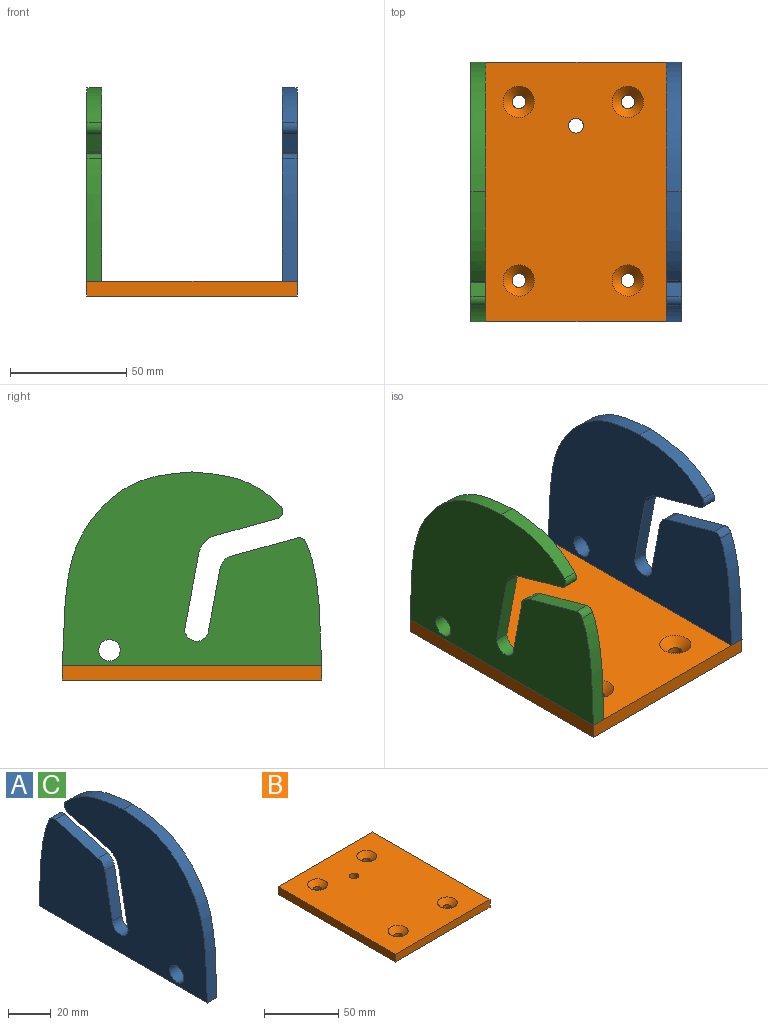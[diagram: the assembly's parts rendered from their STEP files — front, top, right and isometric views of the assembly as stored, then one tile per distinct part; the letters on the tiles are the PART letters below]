
ASSEMBLY  parts=3 mates=2
PART A: 16 faces, bbox 6.4x111.8x83.3 mm
  f0: cylinder r=3.17mm len=6.35mm, axis (-1,0,0), area 41.8mm2, adj f1,f13,f14,f15
  f1: extruded ~38.25x14.72mm, area 267.7mm2, adj f0,f2,f14,f15
  f2: extruded ~83.31x55.88mm, area 730.4mm2, adj f1,f3,f14,f15
  f3: plane 111.76x6.35mm, normal (0,0,-1), area 709.7mm2, adj f2,f4,f14,f15
  f4: extruded ~53.13x6.85mm, area 342.3mm2, adj f3,f5,f14,f15
  f5: cylinder r=3.17mm len=6.35mm, axis (-1,0,0), area 28.5mm2, adj f4,f6,f14,f15
  f6: plane 28.54x7.91mm, normal (0,-0.27,0.96), area 188mm2, adj f5,f7,f14,f15
  f7: cylinder r=6.35mm len=6.35mm, axis (-1,0,0), area 44.9mm2, adj f6,f8,f14,f15
  f8: plane 26.4x6.35mm, normal (0,-0.98,0.18), area 170.6mm2, adj f7,f9,f14,f15
  f9: cylinder r=5.21mm len=10.41mm, axis (-1,0,0), area 103.9mm2, adj f8,f10,f14,f15
  f10: plane 32.79x6.35mm, normal (0,0.98,-0.18), area 211.8mm2, adj f9,f11,f14,f15
  f11: cylinder r=9.53mm len=7.42mm, axis (-1,0,0), area 67.4mm2, adj f10,f13,f14,f15
  f12: cylinder r=4.64mm len=9.27mm, axis (-1,0,0), area 184.9mm2, adj f14,f15
  f13: plane 27.02x7.49mm, normal (0,0.27,-0.96), area 178mm2, adj f0,f11,f14,f15
  f14: plane 111.76x83.31mm, normal (1,0,0), area 7040.6mm2, adj f0,f1,f2,f3,f4,f5,f6,f7
  f15: plane 111.76x83.31mm, normal (-1,0,0), area 7040.6mm2, adj f0,f1,f2,f3,f4,f5,f6,f7
PART B: 15 faces, bbox 90.6x111.8x6.4 mm
  f0: plane 90.55x6.35mm, normal (0,-1,0), area 575mm2, adj f1,f8,f9,f10
  f1: plane 111.76x6.35mm, normal (1,0,0), area 709.7mm2, adj f0,f2,f9,f10
  f2: plane 90.55x6.35mm, normal (0,1,0), area 575mm2, adj f1,f8,f9,f10
  f3: cylinder r=2.92mm len=5.84mm, axis (0,0,-1), area 46.6mm2, adj f10,f14
  f4: cylinder r=2.92mm len=5.84mm, axis (0,0,-1), area 46.6mm2, adj f10,f12
  f5: cylinder r=2.92mm len=5.84mm, axis (0,0,-1), area 46.6mm2, adj f10,f13
  f6: cylinder r=2.92mm len=5.84mm, axis (0,0,-1), area 46.6mm2, adj f10,f11
  f7: cylinder r=3.17mm len=6.35mm, axis (0,0,-1), area 126.7mm2, adj f9,f10
  f8: plane 111.76x6.35mm, normal (-1,0,0), area 709.7mm2, adj f0,f2,f9,f10
  f9: plane 111.76x90.55mm, normal (0,0,1), area 9519mm2, adj f0,f1,f2,f7,f8,f11,f12,f13
  f10: plane 111.76x90.55mm, normal (0,0,-1), area 9981.1mm2, adj f0,f1,f2,f3,f4,f5,f6,f7
  f11: cone r=2.92mm half-angle=45deg, axis (0,0,1), area 163.4mm2, adj f6,f9
  f12: cone r=2.92mm half-angle=45deg, axis (0,0,1), area 163.4mm2, adj f4,f9
  f13: cone r=2.92mm half-angle=45deg, axis (0,0,1), area 163.4mm2, adj f5,f9
  f14: cone r=2.92mm half-angle=45deg, axis (0,0,1), area 163.4mm2, adj f3,f9
PART C: same geometry as A
PLACE A rot(axis=(0,0,1),180deg) t=(90.55,110.09,28.24)mm
PLACE B t=(-255.29,110.09,21.89)mm
PLACE C rot(axis=(0,0,1),180deg) t=(6.35,110.09,28.24)mm
MATE fastened A.f3 <-> B.f9  axis (0,0,-1) through (90.55,110.09,28.24)mm
MATE fastened C.f3 <-> B.f9  axis (0,0,-1) through (6.35,110.09,28.24)mm
